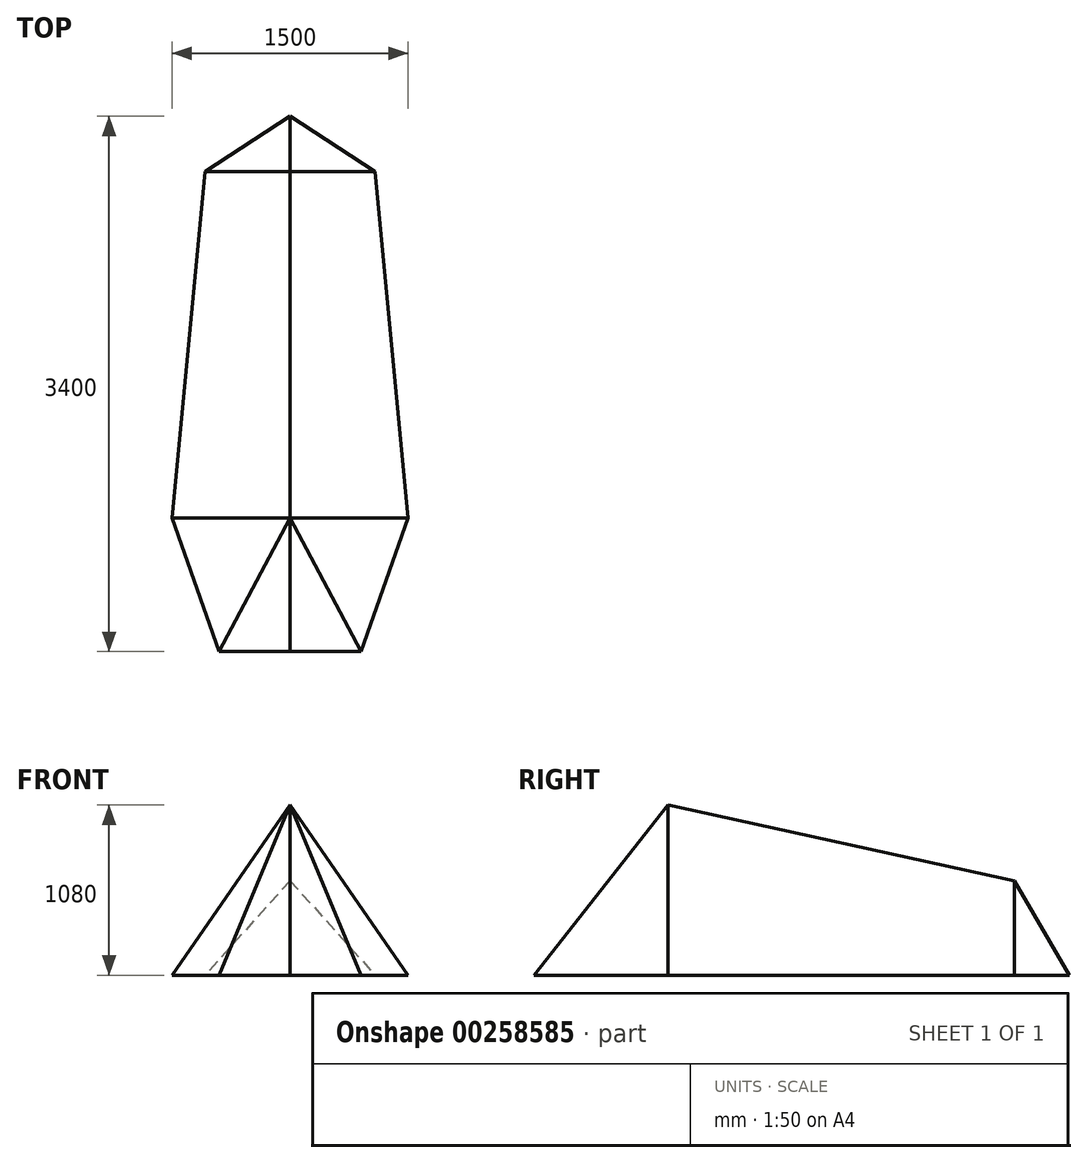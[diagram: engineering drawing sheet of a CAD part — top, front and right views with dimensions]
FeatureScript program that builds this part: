
annotation { "Feature Type Name" : "Feature", "Feature Type Description" : "" }
export const myFeature = defineFeature(function(context is Context, id is Id, definition is map)
    precondition{}
    {
        {
            var Q0;
            Q0=qCreatedBy(makeId("Front.planeOp"),FACE);
            var sketch = newSketch(context, id + "F0", { "sketchPlane" : qUnion([Q0])});
            skLineSegment(sketch, "E0", {"start": v(0, 0) * mm, "end": v(-750, 0) * mm});
            skLineSegment(sketch, "E1", {"start": v(0, 0) * mm, "end": v(0, 1080) * mm});
            skLineSegment(sketch, "E2", {"start": v(0, 1080) * mm, "end": v(-750, 0) * mm});
            skSolve(sketch);
        }
        {
            var Q0;
            Q0=makeQuery(id+"F0.imprint","IMPRINT",FACE,{"disambiguationData":[TD([[makeQuery(id+"F0.imprint","IMPRINT",EDGE,{"derivedFrom":sQuery(id+"F0.wireOp",EDGE,"E0")}),-1.0]])]});
            cPlane(context, id + "F1", {"entities" : qUnion([Q0]), "cplaneType" : CPlaneType.OFFSET, "offset" : 2200 * mm, "oppositeDirection" : true, "width" : 150 * mm, "height" : 150 * mm});
        }
        {
            var Q0;
            Q0=qCreatedBy(id+"F1.planeOp",FACE);
            var sketch = newSketch(context, id + "F2", { "sketchPlane" : qUnion([Q0])});
            skLineSegment(sketch, "E3", {"start": v(0, 0) * mm, "end": v(-540, 0) * mm});
            skLineSegment(sketch, "E4", {"start": v(0, 0) * mm, "end": v(0, 600) * mm});
            skLineSegment(sketch, "E5", {"start": v(0, 600) * mm, "end": v(-540, 0) * mm});
            skSolve(sketch);
        }
        {
            var Q0;
            Q0=sQuery(id+"F0.wireOp",EDGE,"E2");
            var Q1;
            Q1=sQuery(id+"F2.wireOp",EDGE,"E5");
            loft(context, id + "F3", {"bodyType" : ToolBodyType.SURFACE, "wireProfilesArray" : [{ "wireProfileEntities" : qUnion([Q0]) }, { "wireProfileEntities" : qUnion([Q1]) }]});
        }
        {
            var Q0;
            Q0=sQuery(id+"F2.wireOp",EDGE,"E3");
            var Q1;
            Q1=sQuery(id+"F0.wireOp",EDGE,"E0");
            loft(context, id + "F4", {"bodyType" : ToolBodyType.SURFACE, "wireProfilesArray" : [{ "wireProfileEntities" : qUnion([Q0]) }, { "wireProfileEntities" : qUnion([Q1]) }]});
        }
        {
            var Q0;
            Q0=makeQuery(id+"F0.imprint","IMPRINT",FACE,{"disambiguationData":[TD([[makeQuery(id+"F0.imprint","IMPRINT",EDGE,{"derivedFrom":sQuery(id+"F0.wireOp",EDGE,"E0")}),-1.0]])]});
            var Q1;
            Q1 = qBodyType(qCreatedBy(id + "F6" ,EDGE), BodyType.WIRE);
            cPlane(context, id + "F5", {"entities" : qUnion([Q0, Q1]), "cplaneType" : CPlaneType.OFFSET, "offset" : 850 * mm, "width" : 150 * mm, "height" : 150 * mm});
        }
        {
            var Q0;
            Q0=qCreatedBy(id+"F5.planeOp",FACE);
            var sketch = newSketch(context, id + "F6", { "sketchPlane" : qUnion([Q0])});
            skLineSegment(sketch, "E6", {"start": v(0, 0) * mm, "end": v(-450, 0) * mm});
            skSolve(sketch);
        }
        {
            var Q0;
            Q0=sQuery(id+"F6.wireOp",VERTEX,"E6.end");
            var Q1;
            Q1=sQuery(id+"F0.wireOp",EDGE,"E2");
            loft(context, id + "F7", {"bodyType" : ToolBodyType.SURFACE, "wireProfilesArray" : [{ "wireProfileEntities" : qUnion([Q0]) }, { "wireProfileEntities" : qUnion([Q1]) }]});
        }
        {
            var Q0;
            Q0=sQuery(id+"F0.wireOp",VERTEX,"E2.start");
            var Q1;
            Q1=sQuery(id+"F6.wireOp",EDGE,"E6");
            loft(context, id + "F8", {"bodyType" : ToolBodyType.SURFACE, "wireProfilesArray" : [{ "wireProfileEntities" : qUnion([Q0]) }, { "wireProfileEntities" : qUnion([Q1]) }]});
        }
        {
            var Q0;
            Q0=qCreatedBy(id+"F1.planeOp",FACE);
            cPlane(context, id + "F9", {"entities" : qUnion([Q0]), "cplaneType" : CPlaneType.OFFSET, "offset" : 350 * mm, "oppositeDirection" : true, "width" : 150 * mm, "height" : 150 * mm});
        }
        {
            var Q0;
            Q0=qCreatedBy(id+"F9.planeOp",FACE);
            var sketch = newSketch(context, id + "F10", { "sketchPlane" : qUnion([Q0])});
            skPoint(sketch, "E7", {"position": v(0, 0) * mm});
            skSolve(sketch);
        }
        {
            var Q0;
            Q0=sQuery(id+"F2.wireOp",EDGE,"E5");
            var Q1;
            Q1=sQuery(id+"F10.wireOp",VERTEX,"E7");
            loft(context, id + "F11", {"bodyType" : ToolBodyType.SURFACE, "wireProfilesArray" : [{ "wireProfileEntities" : qUnion([Q0]) }, { "wireProfileEntities" : qUnion([Q1]) }]});
        }
        {
            var Q0;
            Q0=makeQuery(id+"F8.opLoft","SWEPT_EDGE",EDGE,{"disambiguationData":[OSD([sQuery(id+"F0.wireOp",VERTEX,"E2.start"),sQuery(id+"F6.wireOp",VERTEX,"E6.start")])]});
            var Q1;
            Q1=makeQuery(id+"F11.opLoft","SWEPT_EDGE",EDGE,{"disambiguationData":[OSD([sQuery(id+"F2.wireOp",VERTEX,"E5.start"),sQuery(id+"F10.wireOp",VERTEX,"E7")])]});
            cPlane(context, id + "F12", {"entities" : qUnion([Q0, Q1]), "cplaneType" : CPlaneType.LINE_ANGLE, "offset" : 25 * mm, "angle" : 0 * degree, "width" : 150 * mm, "height" : 150 * mm});
        }
        {
            var Q0;
            Q0=makeQuery(id+"F4.opLoft","SWEPT_BODY",BODY,{"disambiguationData":[OSD([sQuery(id+"F0.wireOp",EDGE,"E0"),sQuery(id+"F2.wireOp",EDGE,"E3")])]});
            var Q1;
            Q1=makeQuery(id+"F7.opLoft","SWEPT_BODY",BODY,{"disambiguationData":[OSD([sQuery(id+"F0.wireOp",EDGE,"E2"),sQuery(id+"F6.wireOp",VERTEX,"E6.end")])]});
            var Q2;
            Q2=makeQuery(id+"F8.opLoft","SWEPT_BODY",BODY,{"disambiguationData":[OSD([sQuery(id+"F0.wireOp",VERTEX,"E2.start"),sQuery(id+"F6.wireOp",EDGE,"E6")])]});
            var Q3;
            Q3=makeQuery(id+"F3.opLoft","SWEPT_BODY",BODY,{"disambiguationData":[OSD([sQuery(id+"F0.wireOp",EDGE,"E2"),sQuery(id+"F2.wireOp",EDGE,"E5")])]});
            var Q4;
            Q4=makeQuery(id+"F11.opLoft","SWEPT_BODY",BODY,{"disambiguationData":[OSD([sQuery(id+"F2.wireOp",EDGE,"E5"),sQuery(id+"F10.wireOp",VERTEX,"E7")])]});
            var Q5;
            Q5=qCreatedBy(id+"F12.planeOp",FACE);
            mirror(context, id + "F13", {"entities" : qUnion([Q0, Q1, Q2, Q3, Q4]), "mirrorPlane" : qUnion([Q5])});
        }
    });
